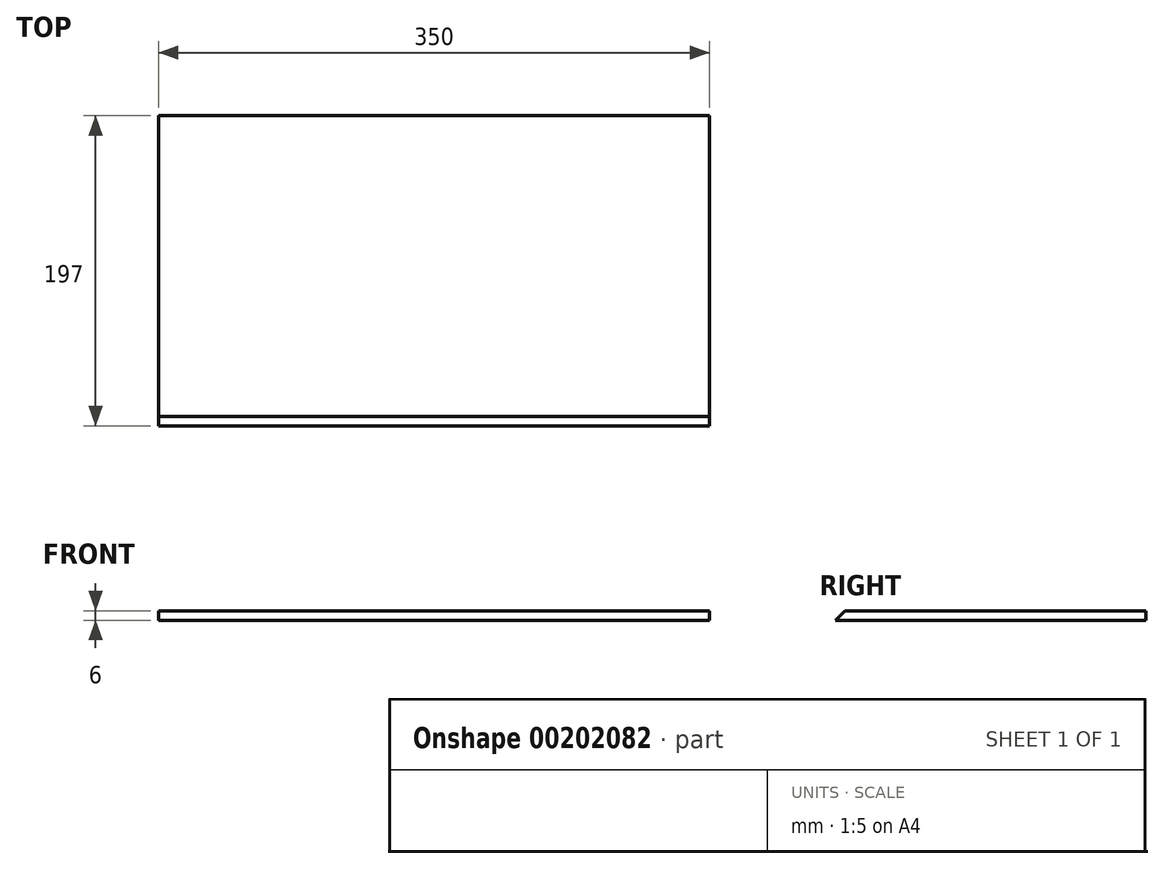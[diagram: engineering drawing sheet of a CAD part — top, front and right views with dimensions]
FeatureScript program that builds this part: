
annotation { "Feature Type Name" : "Feature", "Feature Type Description" : "" }
export const myFeature = defineFeature(function(context is Context, id is Id, definition is map)
    precondition{}
    {
        {
            var Q0;
            Q0=qCreatedBy(makeId("Top.planeOp"),FACE);
            var sketch = newSketch(context, id + "F0", { "sketchPlane" : qUnion([Q0])});
            skLineSegment(sketch, "E0.bottom", {"start": v(278.19, -105.37) * mm, "end": v(-71.81, -105.37) * mm});
            skLineSegment(sketch, "E0.top", {"start": v(278.19, 94.63) * mm, "end": v(-71.81, 94.63) * mm});
            skLineSegment(sketch, "E0.left", {"start": v(278.19, -105.37) * mm, "end": v(278.19, 94.63) * mm});
            skLineSegment(sketch, "E0.right", {"start": v(-71.81, -105.37) * mm, "end": v(-71.81, 94.63) * mm});
            skPoint(sketch, "E0.middle", {"position": v(103.19, -5.37) * mm});
            skSolve(sketch);
        }
        {
            var Q0;
            Q0=qSketchRegion(id+"F0",true);
            extrude(context, id + "F1", {"entities" : qUnion([Q0]), "depth" : 6 * mm});
        }
        {
            var Q0;
            Q0=makeQuery(id+"F1.opExtrude","CAP_EDGE",EDGE,{"disambiguationData":[OSD([sQuery(id+"F0.wireOp",EDGE,"E0.bottom")])],"isStart":false});
            chamfer(context, id + "F2", {"entities" : qUnion([Q0]), "width" : 6 * mm, "tangentPropagation" : true});
        }
        {
            var Q0;
            Q0=makeQuery(id+"F1.opExtrude","SWEPT_FACE",FACE,{"disambiguationData":[OSD([sQuery(id+"F0.wireOp",EDGE,"E0.top")])]});
            extrude(context, id + "F3", {"entities" : qUnion([Q0]), "operationType" : NewBodyOperationType.REMOVE, "oppositeDirection" : true, "depth" : 3 * mm});
        }
    });
